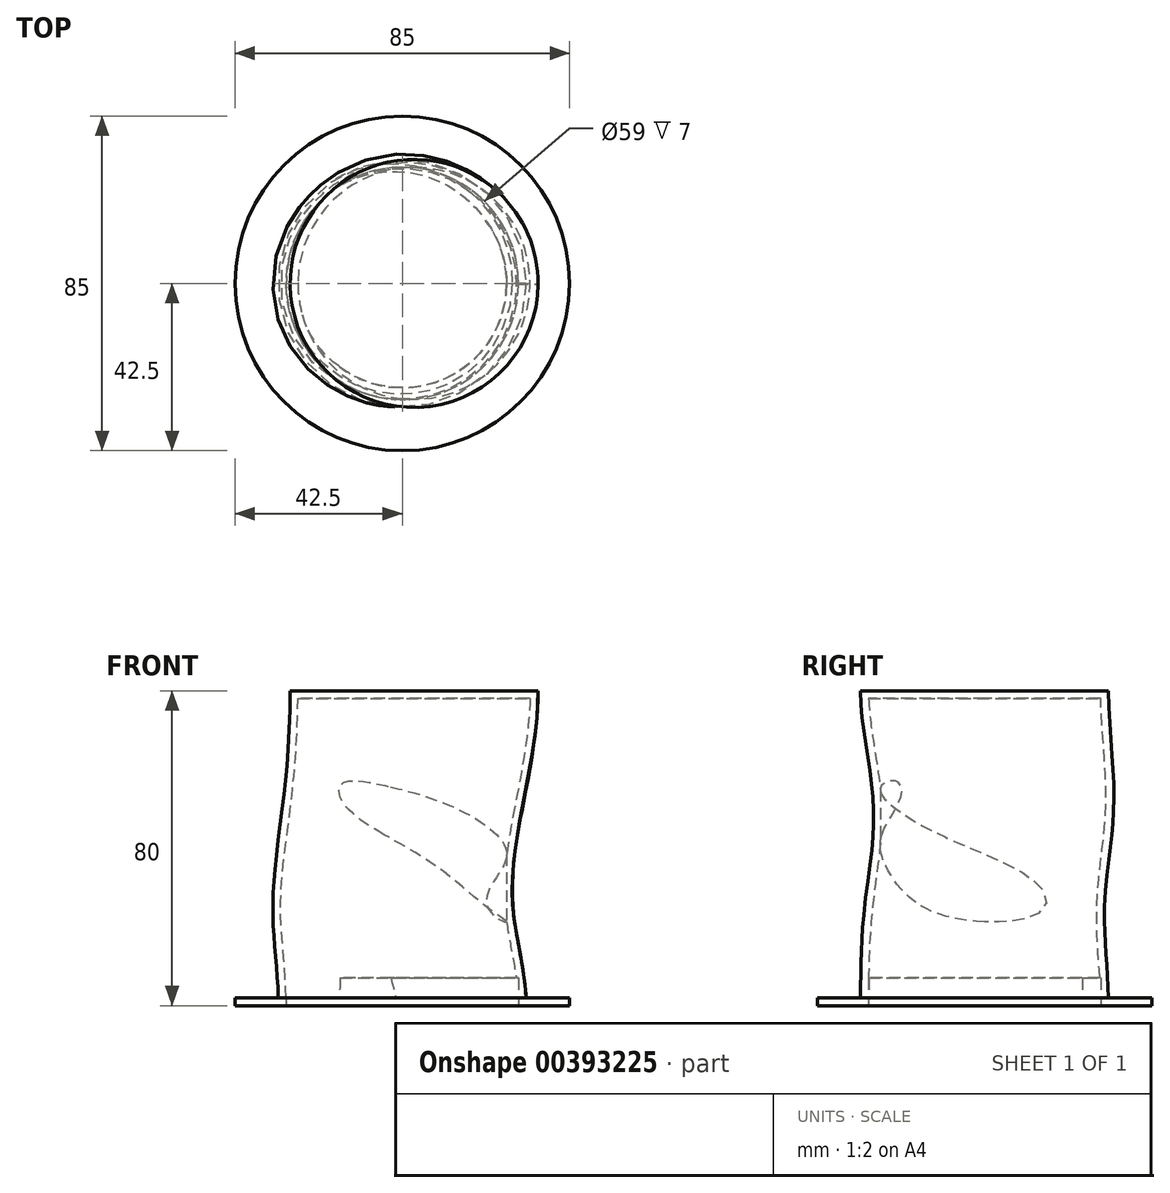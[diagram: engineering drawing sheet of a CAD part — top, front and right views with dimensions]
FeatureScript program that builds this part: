
annotation { "Feature Type Name" : "Feature", "Feature Type Description" : "" }
export const myFeature = defineFeature(function(context is Context, id is Id, definition is map)
    precondition{}
    {
        {
            var Q0;
            Q0=qCreatedBy(makeId("Top.planeOp"),FACE);
            var sketch = newSketch(context, id + "F0", { "sketchPlane" : qUnion([Q0])});
            skCircle(sketch, "E0", {"center": v(0, 0) * mm, "radius": 42.5 * mm});
            skSolve(sketch);
        }
        {
            var Q0;
            Q0=qCreatedBy(makeId("Top.planeOp"),FACE);
            var sketch = newSketch(context, id + "F1", { "sketchPlane" : qUnion([Q0])});
            skCircle(sketch, "E1", {"center": v(0, 0) * mm, "radius": 31.5 * mm});
            skSolve(sketch);
        }
        {
            var Q0;
            Q0=qCreatedBy(makeId("Top.planeOp"),FACE);
            cPlane(context, id + "F2", {"entities" : qUnion([Q0]), "cplaneType" : CPlaneType.OFFSET, "offset" : 25 * mm, "width" : 150 * mm, "height" : 150 * mm});
        }
        {
            var Q0;
            Q0=qCreatedBy(id+"F2.planeOp",FACE);
            var sketch = newSketch(context, id + "F3", { "sketchPlane" : qUnion([Q0])});
            skCircle(sketch, "E2", {"center": v(-2.4, 0) * mm, "radius": 30.5 * mm});
            skSolve(sketch);
        }
        {
            var Q0;
            Q0=qCreatedBy(id+"F2.planeOp",FACE);
            cPlane(context, id + "F4", {"entities" : qUnion([Q0]), "cplaneType" : CPlaneType.OFFSET, "offset" : 25 * mm, "width" : 150 * mm, "height" : 150 * mm});
        }
        {
            var Q0;
            Q0=qCreatedBy(id+"F4.planeOp",FACE);
            var sketch = newSketch(context, id + "F5", { "sketchPlane" : qUnion([Q0])});
            skCircle(sketch, "E3", {"center": v(0, 2.31) * mm, "radius": 30.5 * mm});
            skSolve(sketch);
        }
        {
            var Q0;
            Q0=qCreatedBy(id+"F4.planeOp",FACE);
            cPlane(context, id + "F6", {"entities" : qUnion([Q0]), "cplaneType" : CPlaneType.OFFSET, "offset" : 30 * mm, "width" : 150 * mm, "height" : 150 * mm});
        }
        {
            var Q0;
            Q0=qCreatedBy(id+"F6.planeOp",FACE);
            var sketch = newSketch(context, id + "F7", { "sketchPlane" : qUnion([Q0])});
            skCircle(sketch, "E4", {"center": v(2.98, 0) * mm, "radius": 31.5 * mm});
            skSolve(sketch);
        }
        {
            var Q1;
            Q1 = qSketchRegion(id + "F1", true);
            var Q2;
            Q2 = qSketchRegion(id + "F3", true);
            var Q3;
            Q3 = qSketchRegion(id + "F5", true);
            var Q4;
            Q4 = qSketchRegion(id + "F7", true);
            loft(context, id + "F8", {"startCondition" : LoftEndDerivativeType.NORMAL_TO_PROFILE, "startMagnitude" : 1, "endCondition" : LoftEndDerivativeType.NORMAL_TO_PROFILE, "endMagnitude" : 1, "sheetProfilesArray" : [{ "sheetProfileEntities" : qUnion([Q1]) }, { "sheetProfileEntities" : qUnion([Q2]) }, { "sheetProfileEntities" : qUnion([Q3]) }, { "sheetProfileEntities" : qUnion([Q4]) }]});
        }
        {
            var Q0;
            Q0=makeQuery(id+"F8.opLoft","CAP_FACE",FACE,{"disambiguationData":[OSD([makeQuery(id+"F1.imprint","IMPRINT",FACE,{"disambiguationData":[TD([[makeQuery(id+"F1.imprint","IMPRINT",EDGE,{"derivedFrom":sQuery(id+"F1.wireOp",EDGE,"E1")}),1.0]])]})])],"isStart":true});
            shell(context, id + "F9", {"entities" : qUnion([Q0]), "thickness" : 2 * mm});
        }
        {
            var Q0;
            Q0 = qSketchRegion(id + "F0", true);
            extrude(context, id + "F10", {"entities" : qUnion([Q0]), "operationType" : NewBodyOperationType.ADD, "depth" : 2 * mm});
        }
        {
            var Q0;
            Q0=qCreatedBy(makeId("Top.planeOp"),FACE);
            var sketch = newSketch(context, id + "F11", { "sketchPlane" : qUnion([Q0])});
            skCircle(sketch, "E5", {"center": v(0, 0) * mm, "radius": 26.5 * mm});
            skSolve(sketch);
        }
        {
            var Q0;
            Q0 = qSketchRegion(id + "F11", true);
            extrude(context, id + "F12", {"entities" : qUnion([Q0]), "operationType" : NewBodyOperationType.REMOVE, "depth" : 76 * mm});
        }
        {
            var Q0;
            Q0=qCreatedBy(makeId("Top.planeOp"),FACE);
            var sketch = newSketch(context, id + "F13", { "sketchPlane" : qUnion([Q0])});
            skCircle(sketch, "E6", {"center": v(0, 0) * mm, "radius": 29.5 * mm});
            skSolve(sketch);
        }
        {
            var Q0;
            Q0 = qSketchRegion(id + "F13", true);
            extrude(context, id + "F14", {"entities" : qUnion([Q0]), "operationType" : NewBodyOperationType.REMOVE, "depth" : 7 * mm});
        }
    });
